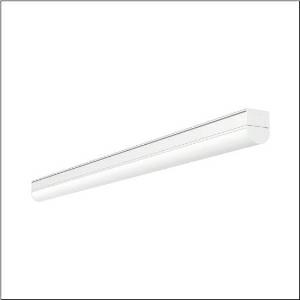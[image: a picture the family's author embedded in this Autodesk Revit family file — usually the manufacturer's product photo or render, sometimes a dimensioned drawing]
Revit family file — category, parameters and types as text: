
# Revit family: ecopack_r__31_51lj12dnm80a_c0ee
name_source: partatom
category: Lighting Fixtures
units: mm (PartAtom-declared; Revit-internal decimal feet)

## family parameters
Cut with Voids When Loaded = No
Host = Face
Light Source = No
Part Type = Normal
Room Calculation Point = No
Round Connector Dimension = Use Diameter
Shared = No

## types (1)
- --- (1 x LED, 6780 lm, 52 W, 5000K)
    Apparent Load = 52 VA
    CIE Flux Codes = 39 67 87 89 100
    Color Rendering = 80
    Color Temperature = 5000K
    Default Elevation = 1800 mm
    Description = Ecopack® 31, diffuser luminaire, primary optical cover: cover, of PC, frosted, light emission: direct distribution, primary light characteristic: symmetric, installation type: surface-mounted, LED, rated luminous flux: 7.000lm, luminous efficacy: 135lm/W, light colour: 830/840/850, colour temperature: 3000/4000/5000K, control gear: DALI 2, with terminal, 5-pole, mains connection: 220..240V, AC, 50/60Hz, rated input power: 52W, housing, of aluminium, traffic white (RAL 9016), length: 1.450mm, width: 56mm, height: 68mm, end cap, of PC, white, protection rating (complete): IP20, insulation class (complete): insulation class I (protective earthing), certification: CE, impact resistance: IK06, permissible operating ambient temperature: -20..+40°C, packaging unit: 1 piece
    Height = 68 mm
    Lamp = 1 x LED
    Lamp Light Flux = 6780 lm
    Lamp Power = 52 W
    Lamp count = 1
    Length = 1450 mm
    Luminous efficacy = 130 lm/W
    Manufacturer = Siteco
    ModVariant = No
    Model = 51LJ12DNM80A
    Mounting Place = Ceiling
    Mounting Type = Surface mounted
    Number of Poles = 1
    OnlyDefault = Yes
    Power Factor = 1
    Product Name = Ecopack® 31
    Product group = diffuser luminaire
    ProductGroupID = 307
    Protection Class = Protection class I
    Protection Degree = IP 20
    RLX_Detail_Level = 1
    RLX_Emergency_Light_Flux = 0 lm
    RLX_Emergency_Type = 0
    RLX_Emergency_Type_DB = No
    RlxData = <blob elided: 21653 chars, md5=e64abef1>
    Socket = socket
    Standby Power = 0 W
    System Light Flux = 6780 lm
    System Power = 52 W
    Type Comments = individual setting: colour temperature 5000K
    Type Image = l_1007033.jpg
    URL = http://relux.com
    VarID = @adj_195417
    Voltage = 0 V
    Weight = 0.00 kg
    Width = 56 mm

## geometry (parser evidence)
native form markers: Blend x4, Sweep x11
no freeform markers — native parametric forms only
